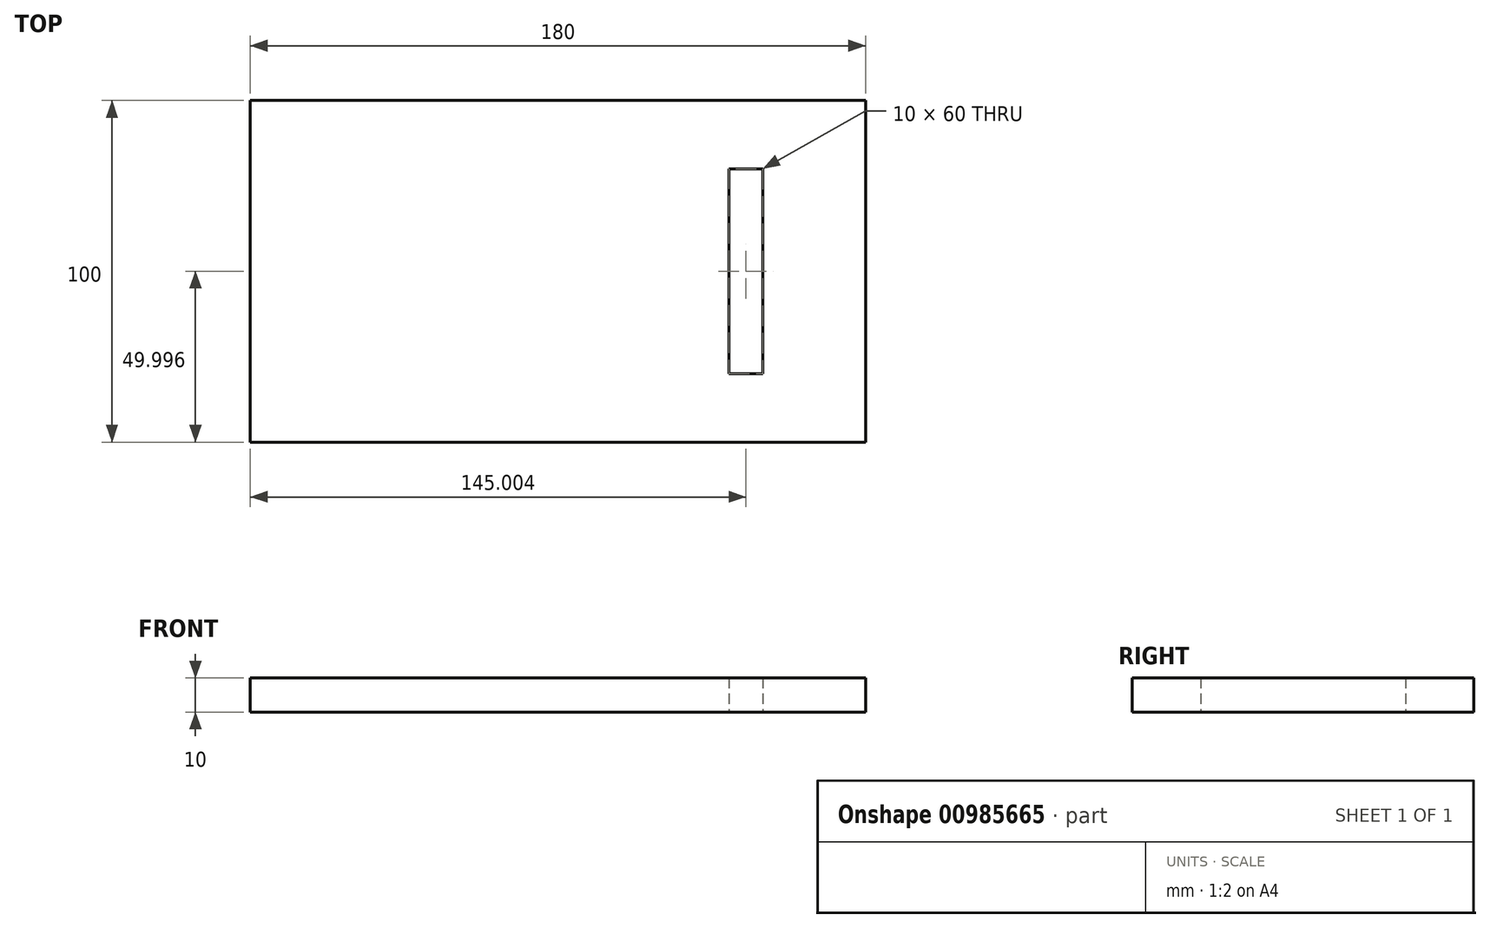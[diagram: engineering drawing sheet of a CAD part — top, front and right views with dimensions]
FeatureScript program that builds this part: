
annotation { "Feature Type Name" : "Feature", "Feature Type Description" : "" }
export const myFeature = defineFeature(function(context is Context, id is Id, definition is map)
    precondition{}
    {
        {
            var Q0;
            Q0=qCreatedBy(makeId("Top.planeOp"),FACE);
            var sketch = newSketch(context, id + "F0", { "sketchPlane" : qUnion([Q0])});
            skLineSegment(sketch, "E0.bottom", {"start": v(-83.13, 48.74) * mm, "end": v(96.87, 48.74) * mm});
            skLineSegment(sketch, "E0.top", {"start": v(-83.13, -51.26) * mm, "end": v(96.87, -51.26) * mm});
            skLineSegment(sketch, "E0.left", {"start": v(-83.13, 48.74) * mm, "end": v(-83.13, -51.26) * mm});
            skLineSegment(sketch, "E0.right", {"start": v(96.87, 48.74) * mm, "end": v(96.87, -51.26) * mm});
            skLineSegment(sketch, "E1.bottom", {"start": v(56.87, 28.74) * mm, "end": v(66.87, 28.74) * mm});
            skLineSegment(sketch, "E1.top", {"start": v(56.87, -31.26) * mm, "end": v(66.87, -31.26) * mm});
            skLineSegment(sketch, "E1.left", {"start": v(56.87, 28.74) * mm, "end": v(56.87, -31.26) * mm});
            skLineSegment(sketch, "E1.right", {"start": v(66.87, 28.74) * mm, "end": v(66.87, -31.26) * mm});
            skSolve(sketch);
        }
        {
            var Q0;
            Q0 = qSketchRegion(id + "F0", true);
            extrude(context, id + "F1", {"entities" : qUnion([Q0]), "depth" : 10 * mm, "offsetDistance" : 25 * mm});
        }
    });
